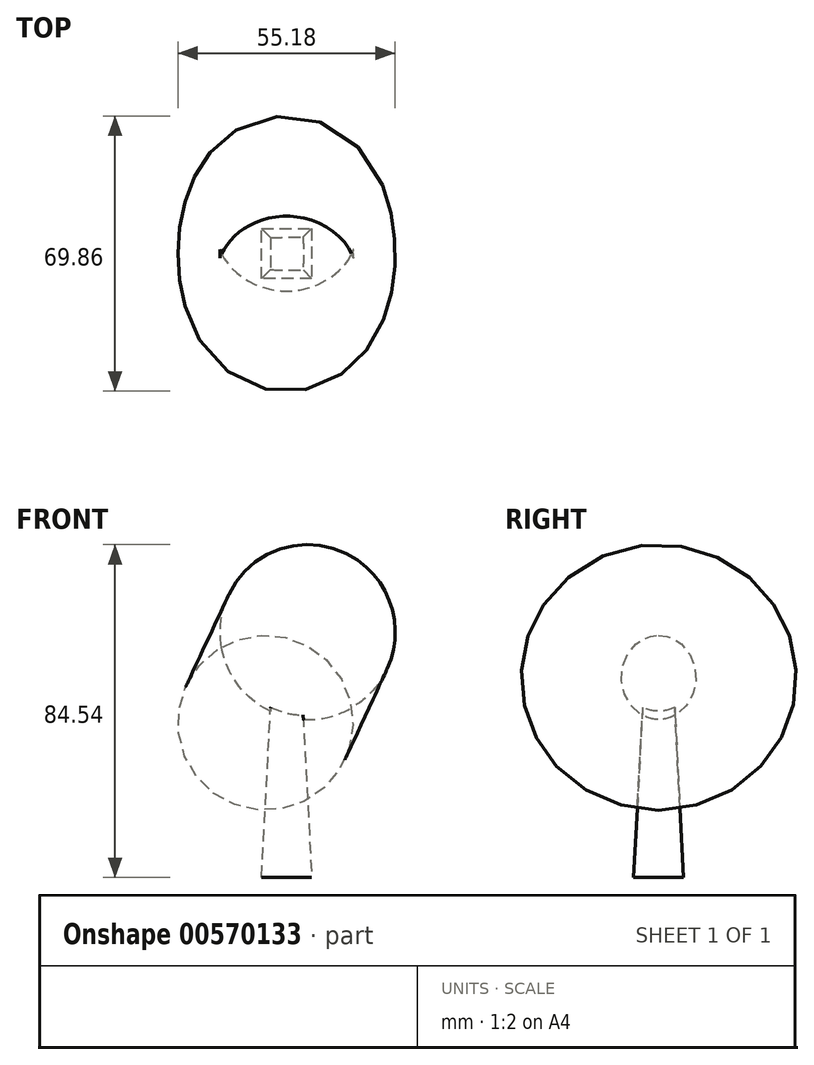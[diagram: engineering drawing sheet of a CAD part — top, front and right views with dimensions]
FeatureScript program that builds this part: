
annotation { "Feature Type Name" : "Feature", "Feature Type Description" : "" }
export const myFeature = defineFeature(function(context is Context, id is Id, definition is map)
    precondition{}
    {
        {
            var Q0;
            Q0=qCreatedBy(makeId("Top.planeOp"),FACE);
            var sketch = newSketch(context, id + "F0", { "sketchPlane" : qUnion([Q0])});
            skLineSegment(sketch, "E0.bottom", {"start": v(-6.35, 6.35) * mm, "end": v(6.35, 6.35) * mm});
            skLineSegment(sketch, "E0.top", {"start": v(-6.35, -6.35) * mm, "end": v(6.35, -6.35) * mm});
            skLineSegment(sketch, "E0.left", {"start": v(-6.35, 6.35) * mm, "end": v(-6.35, -6.35) * mm});
            skLineSegment(sketch, "E0.right", {"start": v(6.35, 6.35) * mm, "end": v(6.35, -6.35) * mm});
            skSolve(sketch);
        }
        {
            var Q0;
            Q0 = qSketchRegion(id + "F0", true);
            extrude(context, id + "F1", {"entities" : qUnion([Q0]), "depth" : 50.8 * mm, "offsetDistance" : 25.4 * mm, "hasDraft" : true, "draftAngle" : 3 * degree, "draftPullDirection" : true});
        }
        {
            var Q0;
            Q0=qCreatedBy(makeId("Front.planeOp"),FACE);
            var sketch = newSketch(context, id + "F2", { "sketchPlane" : qUnion([Q0])});
            skLineSegment(sketch, "E1", {"start": v(-31.1, 65.3) * mm, "end": v(0, 50.8) * mm, "construction": true});
            skLineSegment(sketch, "E2", {"start": v(14.65, 82.2) * mm, "end": v(-19.52, 8.94) * mm, "construction": true});
            skPoint(sketch, "E3", {"position": v(-5.37, 39.29) * mm});
            skLineSegment(sketch, "E4", {"start": v(-31.1, 65.3) * mm, "end": v(39.64, 32.32) * mm, "construction": true});
            skArc(sketch, "E5", {"start": v(16.53, 43.1) * mm, "mid": v(4.03, 59.43) * mm, "end": v(-16.53, 58.5) * mm});
            skLineSegment(sketch, "E6", {"start": v(-16.53, 58.5) * mm, "end": v(16.53, 43.1) * mm});
            skSolve(sketch);
        }
        {
            var Q0;
            Q0 = qSketchRegion(id + "F2", true);
            var Q1;
            Q1=sQuery(id+"F2.wireOp",EDGE,"E4");
            revolve(context, id + "F3", {"operationType" : NewBodyOperationType.ADD, "entities" : qUnion([Q0]), "axis" : qUnion([Q1]), "revolveType" : RevolveType.FULL});
        }
    });
